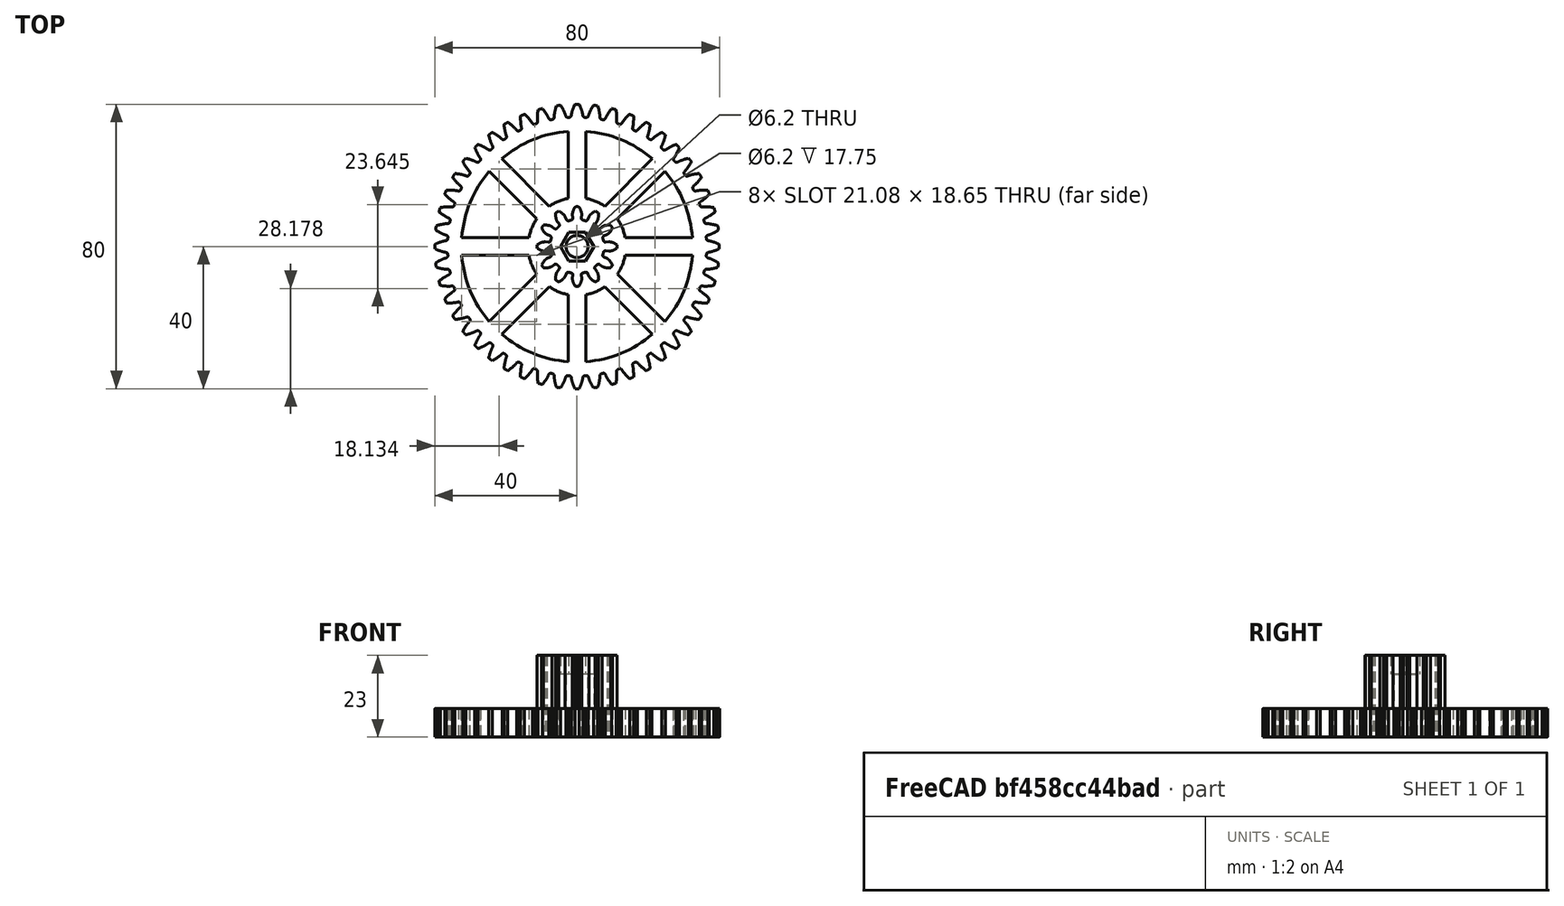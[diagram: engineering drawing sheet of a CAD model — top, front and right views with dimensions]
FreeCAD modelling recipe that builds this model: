
FCSTD DOCUMENT  (FreeCAD 0.20R29177 (Git))
Label: TOP_-_Part_5C_-_DoubleGear
License: All rights reserved
LicenseURL: http://en.wikipedia.org/wiki/All_rights_reserved
objects: Part::Part2DObjectPython×3, Part::Extrusion×3, Part::Cut×3, Mesh::Feature×1, Part::Cylinder×1, Sketcher::SketchObject×1, PartDesign::FeatureBase×1, PartDesign::Pocket×1, PartDesign::PolarPattern×1, PartDesign::Body×1, Part::RegularPolygon×1
note: 17 computed .brp shape members not serialized (recipe doc carries the construction recipe); baked Part::Feature solids carry a one-line shape summary decoded from their .brp

FEATURE [Mesh::Feature] TOP___Part_5C___DoubleGear  label="TOP_-_Part_5C_-_DoubleGear"
  Placement = pos=(88.45,-90.1,-31) rot=(0,0,1;0rad)
FEATURE [Part::Part2DObjectPython] InvoluteGear  label="InvoluteGear12t"  # Draft 2D object (typed FeaturePython)
  ExternalGear = true
  HighPrecision = false
  Modules = 1.6
  NumberOfTeeth = 12
  PressureAngle = 20
FEATURE [Part::Part2DObjectPython] InvoluteGear001  label="InvoluteGear30t"  # Draft 2D object (typed FeaturePython)
  ExternalGear = true
  HighPrecision = false
  Modules = 1.6
  NumberOfTeeth = 30
  Placement = pos=(0,0,0) rot=(0,0,1;0.314159rad)
  PressureAngle = 20
FEATURE [Part::Part2DObjectPython] InvoluteGear002  label="InvoluteGear48t"  # Draft 2D object (typed FeaturePython)
  ExternalGear = true
  HighPrecision = false
  Modules = 1.6
  NumberOfTeeth = 48
  Placement = pos=(0,0,-15) rot=(0,0,1;0rad)
  PressureAngle = 20
FEATURE [Part::Extrusion] Extrude001
  Base = -> InvoluteGear002
  Dir = (0,0,1)
  DirMode = 2
  FaceMakerClass = Part::FaceMakerBullseye
  LengthFwd = 8
  LengthRev = 0
  Reversed = true
  Solid = true
  Symmetric = false
FEATURE [Part::Extrusion] Extrude
  Base = -> InvoluteGear
  Dir = (0,0,1)
  DirMode = 2
  FaceMakerClass = Part::FaceMakerBullseye
  LengthFwd = 23
  LengthRev = 0
  Reversed = true
  Solid = true
  Symmetric = false
FEATURE [Part::Cylinder] Cylinder
  Angle = 360
  AttacherType = Attacher::AttachEngine3D
  FirstAngle = 0
  Height = 24
  Placement = pos=(0,0,-23.5) rot=(0,0,1;0rad)
  Radius = 3.1
  SecondAngle = 0
FEATURE [Part::Cut] Cut
  Base = -> Extrude
  Tool = -> Cylinder
FEATURE [Part::Cut] Cut001
  Base = -> Extrude001
  Tool = -> Cylinder
FEATURE [Sketcher::SketchObject] Sketch001
  FullyConstrained = false
  MapMode = 5
  Support = -> [XY_Plane]
  sketch-geometry (4):
    g0: ArcOfCircle CenterX=0 CenterY=-4.27746e-07 CenterZ=0 NormalX=0 NormalY=0 NormalZ=1 AngleXU=0 Radius=32.5 StartAngle=1.6478 EndAngle=2.2792
    g1: ArcOfCircle CenterX=0 CenterY=0 CenterZ=0 NormalX=0 NormalY=0 NormalZ=1 AngleXU=0 Radius=13.75 StartAngle=1.75363 EndAngle=2.17336
    g2: LineSegment StartX=-2.5 StartY=32.4037 StartZ=0 EndX=-2.5 EndY=13.5208 EndZ=0
    g3: LineSegment StartX=-7.79289 StartY=11.3284 StartZ=0 EndX=-21.1451 EndY=24.6806 EndZ=0
  constraints (8):
    c: DistanceX(g0,g-1) = 2.5
    c: Diameter(g0) = 65
    c: Diameter(g1) = 27.5
    c: Coincident(g2,g0)
    c: Coincident(g2,g1)
    c: Vertical(g2)
    c: Coincident(g3,g1)
    c: Coincident(g3,g0)
FEATURE [PartDesign::FeatureBase] BaseFeature
  BaseFeature = -> Cut001
FEATURE [PartDesign::Pocket] Pocket
  BaseFeature = -> BaseFeature
  Direction = (0,0,-1)
  Length = 22
  Length2 = 5
  Profile = -> Sketch001
  ReferenceAxis = -> Sketch001 [N_Axis]
  Type = 1
FEATURE [PartDesign::PolarPattern] PolarPattern
  Angle = 360
  Axis = -> Sketch001 [N_Axis]
  BaseFeature = -> Pocket
  Occurrences = 8
  Originals = -> [Pocket]
FEATURE [PartDesign::Body] Body
  BaseFeature = -> Cut001
  Group = -> [BaseFeature,Extrude001,Extrude,Sketch001,Pocket,PolarPattern]
  Origin = -> Origin
  Tip = -> PolarPattern
FEATURE [Part::RegularPolygon] RegularPolygon001  label="Regular polygon001"
  AttacherType = Attacher::AttachEngine3D
  Circumradius = 4.7
  Polygon = 6
FEATURE [Part::Extrusion] Extrude002
  Base = -> RegularPolygon001
  Dir = (0,0,1)
  DirMode = 2
  FaceMakerClass = Part::FaceMakerBullseye
  LengthFwd = 5.25
  LengthRev = 0
  Reversed = true
  Solid = true
  Symmetric = false
FEATURE [Part::Cut] Cut002
  Base = -> Cut
  Tool = -> Extrude002
